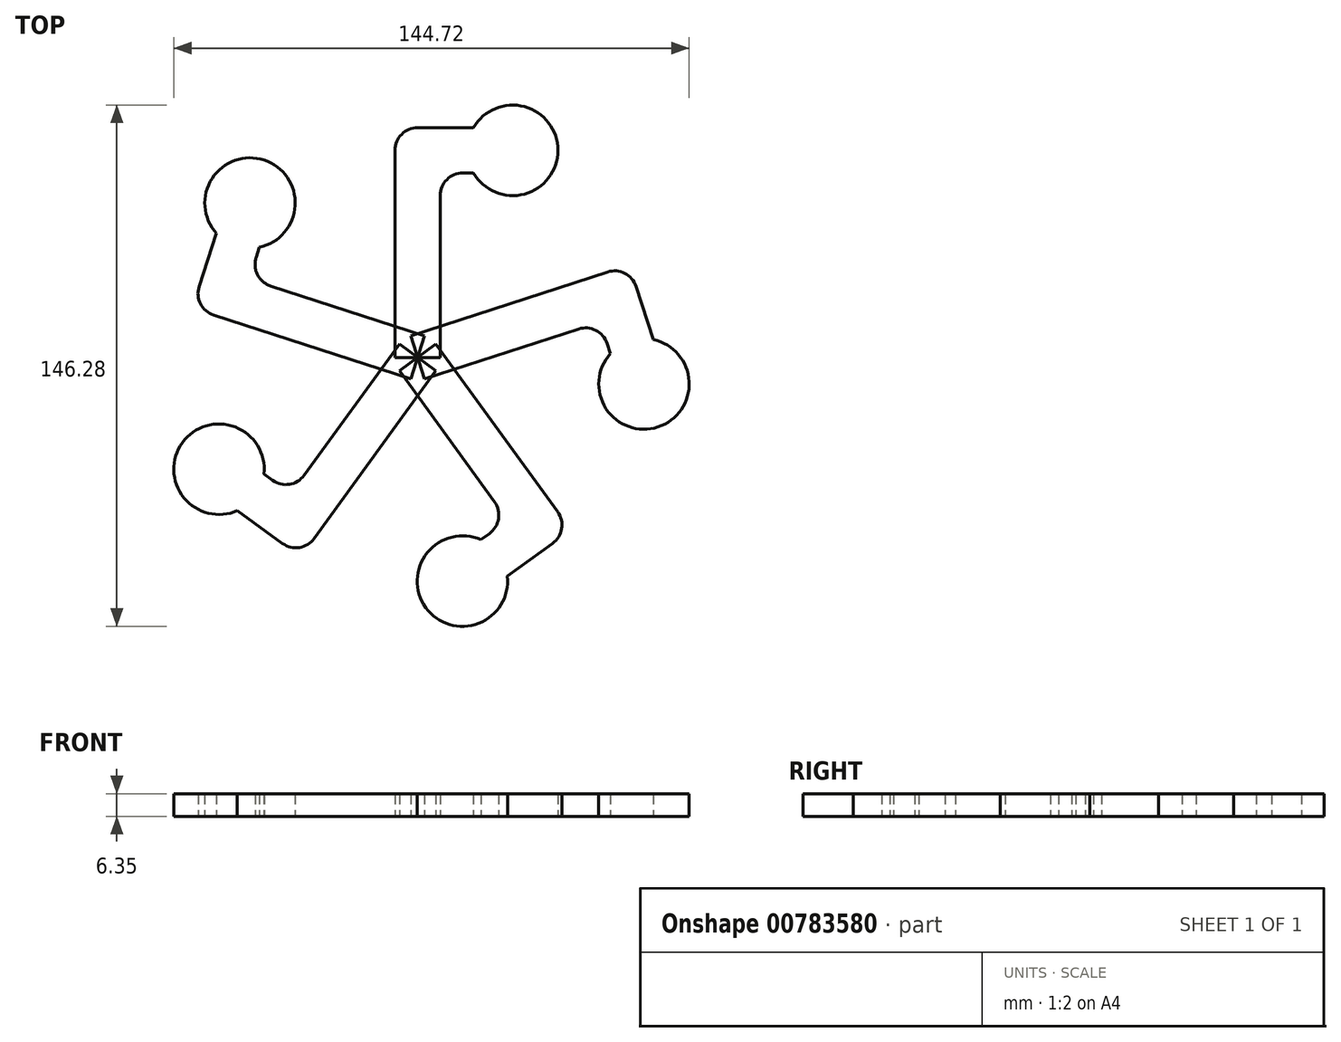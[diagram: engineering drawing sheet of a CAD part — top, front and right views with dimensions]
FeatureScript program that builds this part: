
annotation { "Feature Type Name" : "Feature", "Feature Type Description" : "" }
export const myFeature = defineFeature(function(context is Context, id is Id, definition is map)
    precondition{}
    {
        {
            var Q0;
            Q0=qCreatedBy(makeId("Top.planeOp"),FACE);
            var sketch = newSketch(context, id + "F0", { "sketchPlane" : qUnion([Q0])});
            skLineSegment(sketch, "E0.0", {"start": v(12.7, 51.8) * mm, "end": v(15.7, 51.8) * mm});
            skLineSegment(sketch, "E1.0", {"start": v(6.35, 0) * mm, "end": v(6.35, 45.45) * mm});
            skLineSegment(sketch, "E2.0", {"start": v(-6.35, 0) * mm, "end": v(-6.35, 58.15) * mm});
            skLineSegment(sketch, "E3.0", {"start": v(0, 64.5) * mm, "end": v(15.7, 64.5) * mm});
            skArc(sketch, "E4.filletArc", {"start": v(0, 64.5) * mm, "mid": v(-4.5, 62.64) * mm, "end": v(-6.35, 58.15) * mm});
            skArc(sketch, "E5.filletArc", {"start": v(12.7, 51.8) * mm, "mid": v(8.2, 49.94) * mm, "end": v(6.35, 45.45) * mm});
            skLineSegment(sketch, "E6", {"start": v(-6.35, 0) * mm, "end": v(6.35, 0) * mm});
            skPoint(sketch, "E7", {"position": v(26.69, 58.15) * mm});
            skCircle(sketch, "E8", {"center": v(26.69, 58.15) * mm, "radius": 12.7 * mm});
            skSolve(sketch);
        }
        {
            var Q0;
            Q0 = qSketchRegion(id + "F0", true);
            extrude(context, id + "F1", {"entities" : qUnion([Q0]), "depth" : 6.35 * mm, "offsetDistance" : 25.4 * mm});
        }
        {
            var Q0;
            Q0=qCreatedBy(makeId("Right.planeOp"),FACE);
            var sketch = newSketch(context, id + "F2", { "sketchPlane" : qUnion([Q0])});
            skLineSegment(sketch, "E9", {"start": v(0, 0) * mm, "end": v(0, 49.57) * mm});
            skSolve(sketch);
        }
        {
            var Q0;
            Q0=makeQuery(id+"F1.opExtrude","SWEPT_BODY",BODY,{"disambiguationData":[OSD([sQuery(id+"F0.wireOp",EDGE,"QuxXVNvQ-RgSI-eEx2-24oe-8oqEmTtYgdey"),sQuery(id+"F0.wireOp",EDGE,"E0.0"),sQuery(id+"F0.wireOp",EDGE,"E1.0"),sQuery(id+"F0.wireOp",EDGE,"E2.0"),sQuery(id+"F0.wireOp",EDGE,"E3.0"),sQuery(id+"F0.wireOp",EDGE,"E4.filletArc"),sQuery(id+"F0.wireOp",EDGE,"E5.filletArc"),sQuery(id+"F0.wireOp",EDGE,"E6")])]});
            var Q1;
            Q1=sQuery(id+"F2.wireOp",EDGE,"E9");
            circularPattern(context, id + "F3", {"entities" : qUnion([Q0]), "axis" : qUnion([Q1]), "angle" : 360 * degree, "instanceCount" : 5, "equalSpace" : true});
        }
    });
